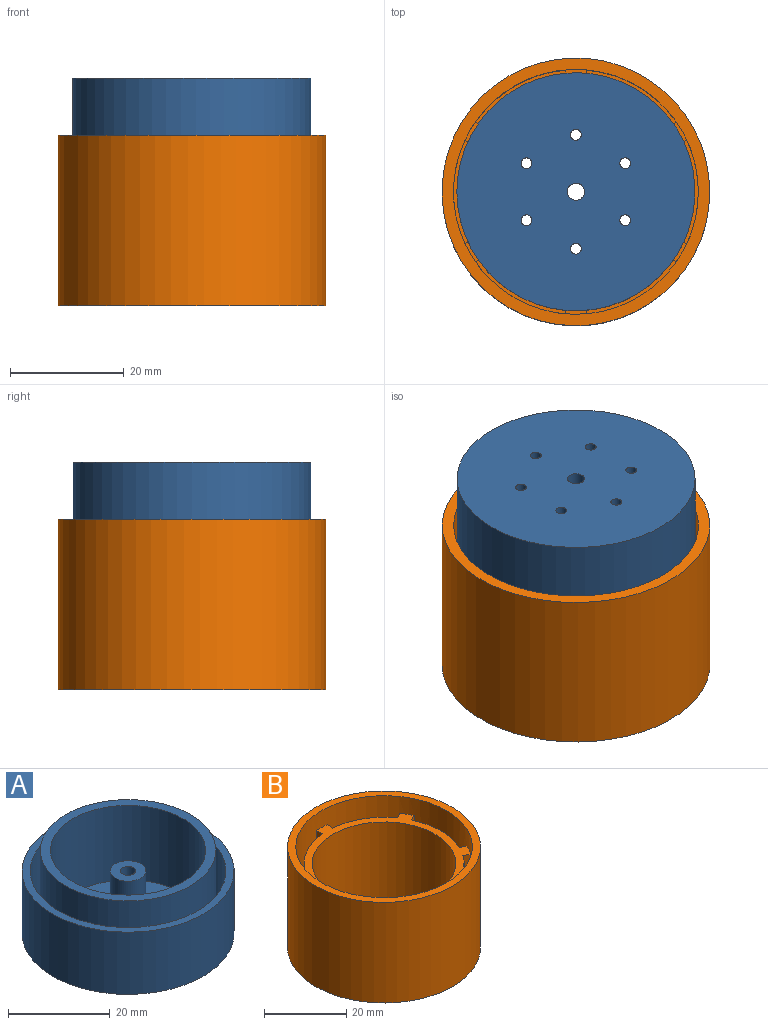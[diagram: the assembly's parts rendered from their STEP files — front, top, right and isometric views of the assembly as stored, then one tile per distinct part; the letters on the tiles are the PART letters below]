
ASSEMBLY  parts=2 mates=1
PART A: 18 faces, bbox 41.8x41.8x20 mm
  f0: cylinder r=1.5mm len=15mm, axis (0,0,-1), area 141.4mm2, adj f2,f3
  f1: cylinder r=3.5mm len=13mm, axis (0,0,-1), area 285.9mm2, adj f2,f4
  f2: plane 7x7mm, normal (0,0,1), area 31.4mm2, adj f0,f1
  f3: plane 41.8x41.8mm, normal (0,0,-1), area 1348.2mm2, adj f0,f10,f12,f13,f14,f15,f16,f17
  f4: plane 30.6x30.6mm, normal (0,0,1), area 679.9mm2, adj f1,f5,f12,f13,f14,f15,f16,f17
  f5: cylinder r=15.3mm len=30.6mm, axis (0,0,-1), area 1730.4mm2, adj f4,f7
  f6: cylinder r=17.3mm len=34.6mm, axis (0,0,-1), area 1956.6mm2, adj f7,f8
  f7: plane 34.6x34.6mm, normal (0,0,1), area 204.8mm2, adj f5,f6
  f8: plane 38.6x38.6mm, normal (0,0,1), area 230mm2, adj f6,f9
  f9: cylinder r=19.3mm len=38.6mm, axis (0,0,-1), area 1576.5mm2, adj f8,f11
  f10: cylinder r=20.9mm len=41.8mm, axis (0,0,-1), area 1969.8mm2, adj f3,f11
  f11: plane 41.8x41.8mm, normal (0,0,1), area 202.1mm2, adj f9,f10
  f12: cylinder r=0.95mm len=2mm, axis (0,0,-1), area 11.9mm2, adj f3,f4
  f13: cylinder r=0.95mm len=2mm, axis (0,0,-1), area 11.9mm2, adj f3,f4
  f14: cylinder r=0.95mm len=2mm, axis (0,0,-1), area 11.9mm2, adj f3,f4
  f15: cylinder r=0.95mm len=2mm, axis (0,0,-1), area 11.9mm2, adj f3,f4
  f16: cylinder r=0.95mm len=2mm, axis (0,0,-1), area 11.9mm2, adj f3,f4
  f17: cylinder r=0.95mm len=2mm, axis (0,0,-1), area 11.9mm2, adj f3,f4
PART B: 30 faces, bbox 47x47x30 mm
  f0: plane 15.91x10.23mm, normal (0,0,1), area 35.8mm2, adj f1,f2,f26,f28
  f1: cylinder r=21.5mm len=43mm, axis (0,0,-1), area 3264.6mm2, adj f0,f3,f5,f7,f9,f11,f15,f17
  f2: cylinder r=19.5mm len=23mm, axis (0,0,-1), area 391.4mm2, adj f0,f15,f26,f28
  f3: plane 18.17x3.83mm, normal (0,0,1), area 35.8mm2, adj f1,f12,f19,f29
  f4: cylinder r=19.5mm len=23mm, axis (0,0,-1), area 391.4mm2, adj f5,f15,f24,f27
  f5: plane 15.91x10.23mm, normal (0,0,1), area 35.8mm2, adj f1,f4,f24,f27
  f6: cylinder r=19.5mm len=23mm, axis (0,0,-1), area 391.4mm2, adj f7,f15,f22,f25
  f7: plane 18.17x3.83mm, normal (0,0,1), area 35.8mm2, adj f1,f6,f22,f25
  f8: cylinder r=19.5mm len=23mm, axis (0,0,-1), area 391.4mm2, adj f9,f15,f20,f23
  f9: plane 15.91x10.23mm, normal (0,0,1), area 35.8mm2, adj f1,f8,f20,f23
  f10: cylinder r=19.5mm len=23mm, axis (0,0,-1), area 391.4mm2, adj f11,f15,f18,f21
  f11: plane 15.91x10.23mm, normal (0,0,1), area 35.8mm2, adj f1,f10,f18,f21
  f12: cylinder r=19.5mm len=23mm, axis (0,0,-1), area 391.4mm2, adj f3,f15,f19,f29
  f13: plane 47x47mm, normal (0,0,-1), area 772.8mm2, adj f14,f16
  f14: cylinder r=17.5mm len=35mm, axis (0,0,-1), area 2748.9mm2, adj f13,f15
  f15: plane 43x39mm, normal (0,0,1), area 275.4mm2, adj f1,f2,f4,f6,f8,f10,f12,f14
  f16: cylinder r=23.5mm len=47mm, axis (0,0,-1), area 4429.6mm2, adj f13,f17
  f17: plane 47x47mm, normal (0,0,1), area 282.7mm2, adj f1,f16
  f18: plane 23x1.64mm, normal (-0.57,0.82,0), area 46mm2, adj f1,f10,f11,f15
  f19: plane 23x1.81mm, normal (0.42,-0.91,0), area 46mm2, adj f1,f3,f12,f15
  f20: plane 23x1.99mm, normal (-1,-0.09,0), area 46mm2, adj f1,f8,f9,f15
  f21: plane 23x1.99mm, normal (1,-0.09,0), area 46mm2, adj f1,f10,f11,f15
  f22: plane 23x1.81mm, normal (-0.42,-0.91,0), area 46mm2, adj f1,f6,f7,f15
  f23: plane 23x1.64mm, normal (0.57,0.82,0), area 46mm2, adj f1,f8,f9,f15
  f24: plane 23x1.64mm, normal (0.57,-0.82,0), area 46mm2, adj f1,f4,f5,f15
  f25: plane 23x1.81mm, normal (-0.42,0.91,0), area 46mm2, adj f1,f6,f7,f15
  f26: plane 23x1.99mm, normal (1,0.09,0), area 46mm2, adj f0,f1,f2,f15
  f27: plane 23x1.99mm, normal (-1,0.09,0), area 46mm2, adj f1,f4,f5,f15
  f28: plane 23x1.64mm, normal (-0.57,-0.82,0), area 46mm2, adj f0,f1,f2,f15
  f29: plane 23x1.81mm, normal (0.42,0.91,0), area 46mm2, adj f1,f3,f12,f15
PLACE A rot(axis=(0,1,0),180deg) t=(-24.1,-1.97,42.92)mm
PLACE B t=(-24.1,-1.97,2.92)mm
MATE fastened A.f10 <-> B.f2  axis (0,0,-1) through (-24.1,-1.97,27.92)mm
